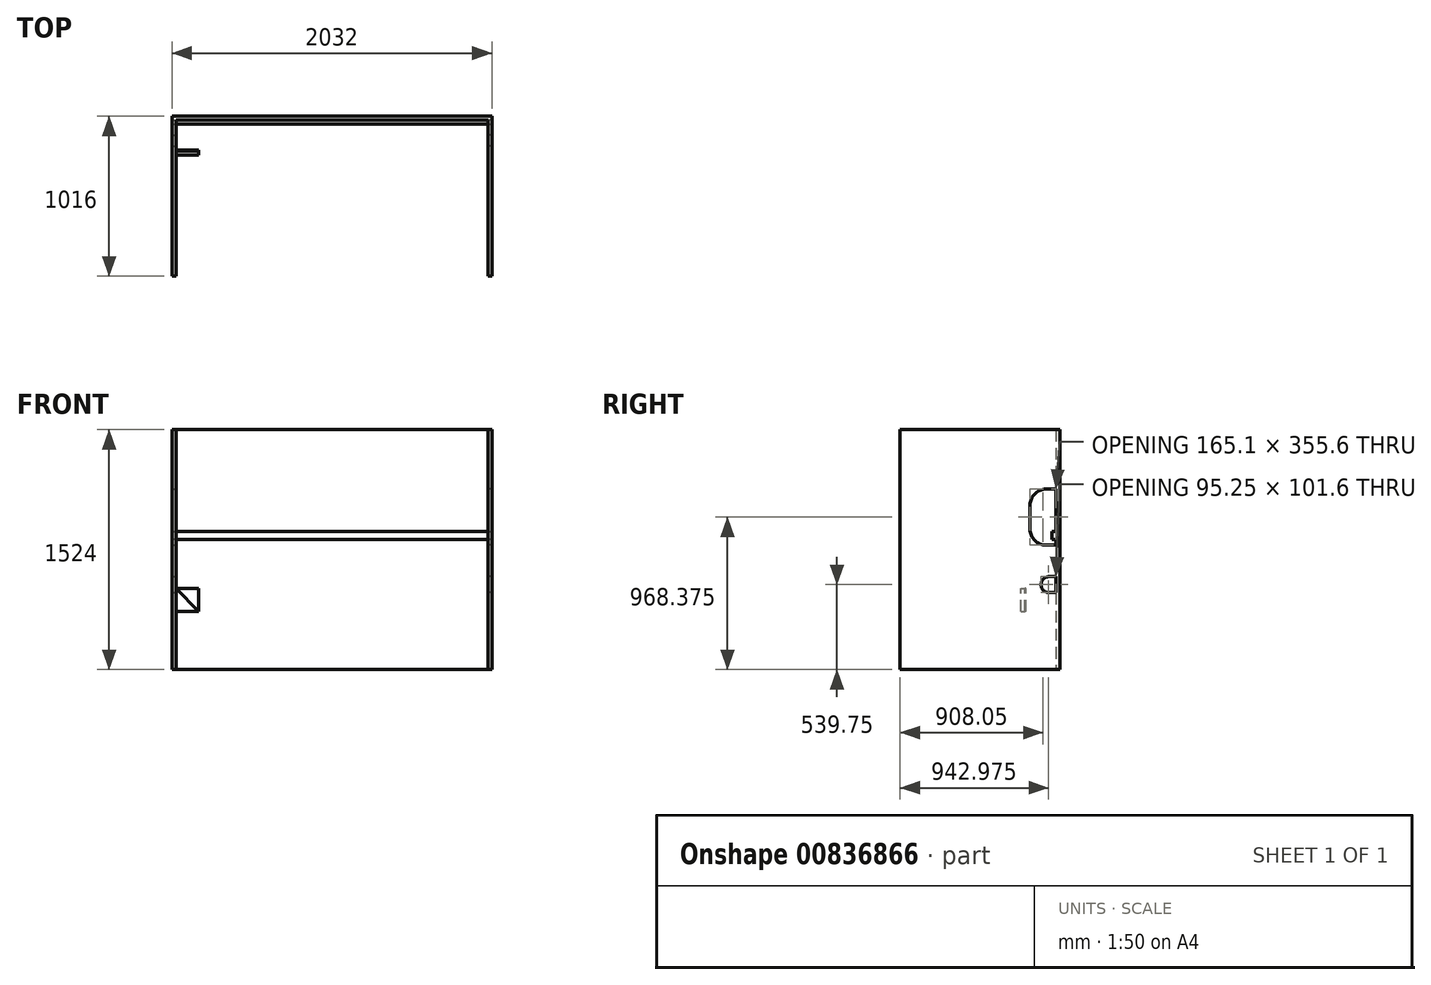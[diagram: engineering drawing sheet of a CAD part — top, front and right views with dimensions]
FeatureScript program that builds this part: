
annotation { "Feature Type Name" : "Feature", "Feature Type Description" : "" }
export const myFeature = defineFeature(function(context is Context, id is Id, definition is map)
    precondition{}
    {
        {
            var Q0;
            Q0=qCreatedBy(makeId("Front.planeOp"),FACE);
            var sketch = newSketch(context, id + "F0", { "sketchPlane" : qUnion([Q0])});
            skLineSegment(sketch, "E0.bottom", {"start": v(1016, 762) * mm, "end": v(-1016, 762) * mm});
            skLineSegment(sketch, "E0.top", {"start": v(1016, -762) * mm, "end": v(-1016, -762) * mm});
            skLineSegment(sketch, "E0.left", {"start": v(1016, 762) * mm, "end": v(1016, -762) * mm});
            skLineSegment(sketch, "E0.right", {"start": v(-1016, 762) * mm, "end": v(-1016, -762) * mm});
            skPoint(sketch, "E0.middle", {"position": v(0, 0) * mm});
            skSolve(sketch);
        }
        {
            var Q0;
            Q0 = qSketchRegion(id + "F0", true);
            extrude(context, id + "F1", {"entities" : qUnion([Q0]), "depth" : 1016 * mm, "offsetDistance" : 25.4 * mm});
        }
        {
            var Q0;
            Q0=makeQuery(id+"F1.opExtrude","CAP_FACE",FACE,{"disambiguationData":[OSD([sQuery(id+"F0.wireOp",EDGE,"E0.bottom"),sQuery(id+"F0.wireOp",EDGE,"E0.top"),sQuery(id+"F0.wireOp",EDGE,"E0.left"),sQuery(id+"F0.wireOp",EDGE,"E0.right")])],"isStart":false});
            var Q1;
            Q1=makeQuery(id+"F1.opExtrude","SWEPT_FACE",FACE,{"disambiguationData":[OSD([sQuery(id+"F0.wireOp",EDGE,"E0.bottom")])]});
            shell(context, id + "F2", {"entities" : qUnion([Q0, Q1]), "thickness" : 25.4 * mm});
        }
        {
            var Q0;
            Q0=makeQuery(id+"F2.opShell","OFFSET_FACE",FACE,{"disambiguationData":[OSD([sQuery(id+"F0.wireOp",EDGE,"E0.right")])]});
            var sketch = newSketch(context, id + "F3", { "sketchPlane" : qUnion([Q0])});
            skLineSegment(sketch, "E1.bottom", {"start": v(-25.4, 28.58) * mm, "end": v(-88.9, 28.58) * mm});
            skLineSegment(sketch, "E1.top", {"start": v(-25.4, 384.18) * mm, "end": v(-88.9, 384.18) * mm});
            skLineSegment(sketch, "E1.left", {"start": v(-25.4, 28.58) * mm, "end": v(-25.4, 384.18) * mm});
            skLineSegment(sketch, "E1.right", {"start": v(-190.5, 130.18) * mm, "end": v(-190.5, 282.58) * mm});
            skPoint(sketch, "E2.visualSharp", {"position": v(-190.5, 384.18) * mm});
            skArc(sketch, "E2.filletArc", {"start": v(-88.9, 384.18) * mm, "mid": v(-160.74, 354.42) * mm, "end": v(-190.5, 282.58) * mm});
            skPoint(sketch, "E3.visualSharp", {"position": v(-190.5, 28.57) * mm});
            skArc(sketch, "E3.filletArc", {"start": v(-190.5, 130.18) * mm, "mid": v(-160.74, 58.33) * mm, "end": v(-88.9, 28.58) * mm});
            skSolve(sketch);
        }
        {
            var Q0;
            Q0 = qSketchRegion(id + "F3", true);
            extrude(context, id + "F4", {"entities" : qUnion([Q0]), "operationType" : NewBodyOperationType.REMOVE, "oppositeDirection" : true, "depth" : 50.8 * mm, "offsetDistance" : 25.4 * mm});
        }
        {
            var Q0;
            Q0=makeQuery(id+"F2.opShell","OFFSET_FACE",FACE,{"disambiguationData":[OSD([sQuery(id+"F0.wireOp",EDGE,"E0.right")])]});
            var sketch = newSketch(context, id + "F5", { "sketchPlane" : qUnion([Q0])});
            skLineSegment(sketch, "E4", {"start": v(-25.4, -736.6) * mm, "end": v(-25.4, -273.05) * mm});
            skLineSegment(sketch, "E5.bottom", {"start": v(-25.4, -273.05) * mm, "end": v(-69.85, -273.05) * mm});
            skLineSegment(sketch, "E5.top", {"start": v(-25.4, -171.45) * mm, "end": v(-69.85, -171.45) * mm});
            skLineSegment(sketch, "E5.left", {"start": v(-25.4, -273.05) * mm, "end": v(-25.4, -171.45) * mm});
            skLineSegment(sketch, "E5.right", {"start": v(-120.65, -222.25) * mm, "end": v(-120.65, -222.25) * mm});
            skPoint(sketch, "E6.visualSharp", {"position": v(-120.65, -171.45) * mm});
            skArc(sketch, "E6.filletArc", {"start": v(-69.85, -171.45) * mm, "mid": v(-105.77, -186.33) * mm, "end": v(-120.65, -222.25) * mm});
            skPoint(sketch, "E7.visualSharp", {"position": v(-120.65, -273.05) * mm});
            skArc(sketch, "E7.filletArc", {"start": v(-120.65, -222.25) * mm, "mid": v(-105.77, -258.17) * mm, "end": v(-69.85, -273.05) * mm});
            skSolve(sketch);
        }
        {
            var Q0;
            Q0 = qSketchRegion(id + "F5", true);
            extrude(context, id + "F6", {"entities" : qUnion([Q0]), "operationType" : NewBodyOperationType.REMOVE, "oppositeDirection" : true, "depth" : 50.8 * mm, "offsetDistance" : 25.4 * mm});
        }
        {
            var Q0;
            Q0=makeQuery(id+"F2.opShell","OFFSET_FACE",FACE,{"disambiguationData":[OSD([sQuery(id+"F0.wireOp",EDGE,"E0.left")])]});
            var sketch = newSketch(context, id + "F7", { "sketchPlane" : qUnion([Q0])});
            skLineSegment(sketch, "E8", {"start": v(25.4, -736.6) * mm, "end": v(25.4, 28.57) * mm});
            skLineSegment(sketch, "E9.bottom", {"start": v(25.4, 28.57) * mm, "end": v(88.9, 28.57) * mm});
            skLineSegment(sketch, "E9.top", {"start": v(25.4, 384.17) * mm, "end": v(88.9, 384.17) * mm});
            skLineSegment(sketch, "E9.left", {"start": v(25.4, 28.57) * mm, "end": v(25.4, 384.17) * mm});
            skLineSegment(sketch, "E9.right", {"start": v(190.5, 130.17) * mm, "end": v(190.5, 282.57) * mm});
            skPoint(sketch, "E10.visualSharp", {"position": v(190.5, 28.57) * mm});
            skArc(sketch, "E10.filletArc", {"start": v(88.9, 28.57) * mm, "mid": v(160.74, 58.33) * mm, "end": v(190.5, 130.17) * mm});
            skPoint(sketch, "E11.visualSharp", {"position": v(190.5, 384.17) * mm});
            skArc(sketch, "E11.filletArc", {"start": v(190.5, 282.57) * mm, "mid": v(160.74, 354.42) * mm, "end": v(88.9, 384.17) * mm});
            skSolve(sketch);
        }
        {
            var Q0;
            Q0 = qSketchRegion(id + "F7", true);
            extrude(context, id + "F8", {"entities" : qUnion([Q0]), "operationType" : NewBodyOperationType.REMOVE, "oppositeDirection" : true, "depth" : 50.8 * mm, "offsetDistance" : 25.4 * mm});
        }
        {
            var Q0;
            Q0=makeQuery(id+"F2.opShell","OFFSET_FACE",FACE,{"disambiguationData":[OSD([sQuery(id+"F0.wireOp",EDGE,"E0.left")])]});
            var sketch = newSketch(context, id + "F9", { "sketchPlane" : qUnion([Q0])});
            skLineSegment(sketch, "E12", {"start": v(25.4, -736.6) * mm, "end": v(25.4, -273.05) * mm});
            skLineSegment(sketch, "E13.bottom", {"start": v(25.4, -273.05) * mm, "end": v(69.85, -273.05) * mm});
            skLineSegment(sketch, "E13.top", {"start": v(25.4, -171.45) * mm, "end": v(69.85, -171.45) * mm});
            skLineSegment(sketch, "E13.left", {"start": v(25.4, -273.05) * mm, "end": v(25.4, -171.45) * mm});
            skLineSegment(sketch, "E13.right", {"start": v(120.65, -222.25) * mm, "end": v(120.65, -222.25) * mm});
            skPoint(sketch, "E14.visualSharp", {"position": v(120.65, -171.45) * mm});
            skArc(sketch, "E14.filletArc", {"start": v(120.65, -222.25) * mm, "mid": v(105.77, -186.33) * mm, "end": v(69.85, -171.45) * mm});
            skPoint(sketch, "E15.visualSharp", {"position": v(120.65, -273.05) * mm});
            skArc(sketch, "E15.filletArc", {"start": v(69.85, -273.05) * mm, "mid": v(105.77, -258.17) * mm, "end": v(120.65, -222.25) * mm});
            skSolve(sketch);
        }
        {
            var Q0;
            Q0 = qSketchRegion(id + "F9", true);
            extrude(context, id + "F10", {"entities" : qUnion([Q0]), "operationType" : NewBodyOperationType.REMOVE, "oppositeDirection" : true, "depth" : 50.8 * mm, "offsetDistance" : 25.4 * mm});
        }
        {
            var Q0;
            Q0=makeQuery(id+"F10.boolean.opBoolean","MERGE",FACE,{"derivedFrom":[makeQuery(id+"F8.boolean.opBoolean","MERGE",FACE,{"derivedFrom":[makeQuery(id+"F6.boolean.opBoolean","MERGE",FACE,{"derivedFrom":[makeQuery(id+"F4.boolean.opBoolean","MERGE",FACE,{"derivedFrom":[makeQuery(id+"F2.opShell","OFFSET_FACE",FACE,{"disambiguationData":[OSD([sQuery(id+"F0.wireOp",EDGE,"E0.bottom"),sQuery(id+"F0.wireOp",EDGE,"E0.top"),sQuery(id+"F0.wireOp",EDGE,"E0.left"),sQuery(id+"F0.wireOp",EDGE,"E0.right")])]})],"fromTools":[makeQuery(id+"F4.opExtrude","SWEPT_FACE",FACE,{"disambiguationData":[OSD([sQuery(id+"F3.wireOp",EDGE,"E1.left")])]})]})],"fromTools":[makeQuery(id+"F6.opExtrude","SWEPT_FACE",FACE,{"disambiguationData":[OSD([sQuery(id+"F5.wireOp",EDGE,"E5.left")])]})]})],"fromTools":[makeQuery(id+"F8.opExtrude","SWEPT_FACE",FACE,{"disambiguationData":[OSD([sQuery(id+"F7.wireOp",EDGE,"E9.left")])]})]})],"fromTools":[makeQuery(id+"F10.opExtrude","SWEPT_FACE",FACE,{"disambiguationData":[OSD([sQuery(id+"F9.wireOp",EDGE,"E13.left")])]})]});
            var sketch = newSketch(context, id + "F11", { "sketchPlane" : qUnion([Q0])});
            skLineSegment(sketch, "E16", {"start": v(-990.6, -736.6) * mm, "end": v(-990.6, 63.5) * mm});
            skLineSegment(sketch, "E17", {"start": v(-990.6, 63.5) * mm, "end": v(-1016, 63.5) * mm});
            skLineSegment(sketch, "E18.bottom", {"start": v(-1016, 63.5) * mm, "end": v(1016, 63.5) * mm});
            skLineSegment(sketch, "E18.top", {"start": v(-1016, 114.3) * mm, "end": v(1016, 114.3) * mm});
            skLineSegment(sketch, "E18.left", {"start": v(-1016, 63.5) * mm, "end": v(-1016, 114.3) * mm});
            skLineSegment(sketch, "E18.right", {"start": v(1016, 63.5) * mm, "end": v(1016, 114.3) * mm});
            skSolve(sketch);
        }
        {
            var Q0;
            Q0 = qSketchRegion(id + "F11", true);
            extrude(context, id + "F12", {"entities" : qUnion([Q0]), "operationType" : NewBodyOperationType.ADD, "depth" : 25.4 * mm, "offsetDistance" : 25.4 * mm});
        }
        {
            var Q0;
            Q0=makeQuery(id+"F2.opShell","OFFSET_FACE",FACE,{"disambiguationData":[OSD([sQuery(id+"F0.wireOp",EDGE,"E0.top")])]});
            var sketch = newSketch(context, id + "F13", { "sketchPlane" : qUnion([Q0])});
            skLineSegment(sketch, "E19.bottom", {"start": v(-990.6, -25.4) * mm, "end": v(990.6, -25.4) * mm});
            skLineSegment(sketch, "E19.top", {"start": v(-990.6, -1016) * mm, "end": v(990.6, -1016) * mm});
            skLineSegment(sketch, "E19.left", {"start": v(-990.6, -25.4) * mm, "end": v(-990.6, -1016) * mm});
            skLineSegment(sketch, "E19.right", {"start": v(990.6, -25.4) * mm, "end": v(990.6, -1016) * mm});
            skSolve(sketch);
        }
        {
            var Q0;
            Q0 = qSketchRegion(id + "F13", true);
            extrude(context, id + "F14", {"entities" : qUnion([Q0]), "operationType" : NewBodyOperationType.REMOVE, "oppositeDirection" : true, "depth" : 50.8 * mm, "offsetDistance" : 25.4 * mm});
        }
        {
            var Q0;
            Q0=makeQuery(id+"F14.boolean.opBoolean","MERGE",FACE,{"derivedFrom":[makeQuery(id+"F2.opShell","OFFSET_FACE",FACE,{"disambiguationData":[OSD([sQuery(id+"F0.wireOp",EDGE,"E0.right")])]})],"fromTools":[makeQuery(id+"F14.opExtrude","SWEPT_FACE",FACE,{"disambiguationData":[OSD([sQuery(id+"F13.wireOp",EDGE,"E19.left")])]})]});
            var sketch = newSketch(context, id + "F15", { "sketchPlane" : qUnion([Q0])});
            skLineSegment(sketch, "E20", {"start": v(-25.4, -762) * mm, "end": v(-215.9, -762) * mm});
            skLineSegment(sketch, "E21", {"start": v(-215.9, -762) * mm, "end": v(-215.9, -393.7) * mm});
            skLineSegment(sketch, "E22.bottom", {"start": v(-215.9, -393.7) * mm, "end": v(-222.25, -393.7) * mm});
            skLineSegment(sketch, "E22.top", {"start": v(-215.9, -247.65) * mm, "end": v(-222.25, -247.65) * mm});
            skLineSegment(sketch, "E22.left", {"start": v(-215.9, -393.7) * mm, "end": v(-215.9, -247.65) * mm});
            skLineSegment(sketch, "E22.right", {"start": v(-222.25, -393.7) * mm, "end": v(-222.25, -247.65) * mm});
            skSolve(sketch);
        }
        {
            var Q0;
            Q0 = qSketchRegion(id + "F15", true);
            extrude(context, id + "F16", {"entities" : qUnion([Q0]), "operationType" : NewBodyOperationType.ADD, "depth" : 142.88 * mm, "offsetDistance" : 25.4 * mm});
        }
        {
            var Q0;
            Q0=makeQuery(id+"F16.opExtrude","SWEPT_FACE",FACE,{"disambiguationData":[OSD([sQuery(id+"F15.wireOp",EDGE,"E22.right")])]});
            var sketch = newSketch(context, id + "F17", { "sketchPlane" : qUnion([Q0])});
            skLineSegment(sketch, "E23", {"start": v(-847.72, -393.7) * mm, "end": v(-990.6, -247.65) * mm});
            skLineSegment(sketch, "E24", {"start": v(-990.6, -247.65) * mm, "end": v(-847.72, -247.65) * mm});
            skLineSegment(sketch, "E25", {"start": v(-847.72, -247.65) * mm, "end": v(-847.72, -393.7) * mm});
            skSolve(sketch);
        }
        {
            var Q0;
            Q0 = qSketchRegion(id + "F17", true);
            extrude(context, id + "F18", {"entities" : qUnion([Q0]), "operationType" : NewBodyOperationType.REMOVE, "oppositeDirection" : true, "depth" : 25.4 * mm, "offsetDistance" : 25.4 * mm});
        }
        {
            var Q0;
            Q0 = qSketchRegion(id + "F17", true);
            extrude(context, id + "F19", {"entities" : qUnion([Q0]), "operationType" : NewBodyOperationType.ADD, "depth" : 25.4 * mm, "offsetDistance" : 25.4 * mm});
        }
    });
